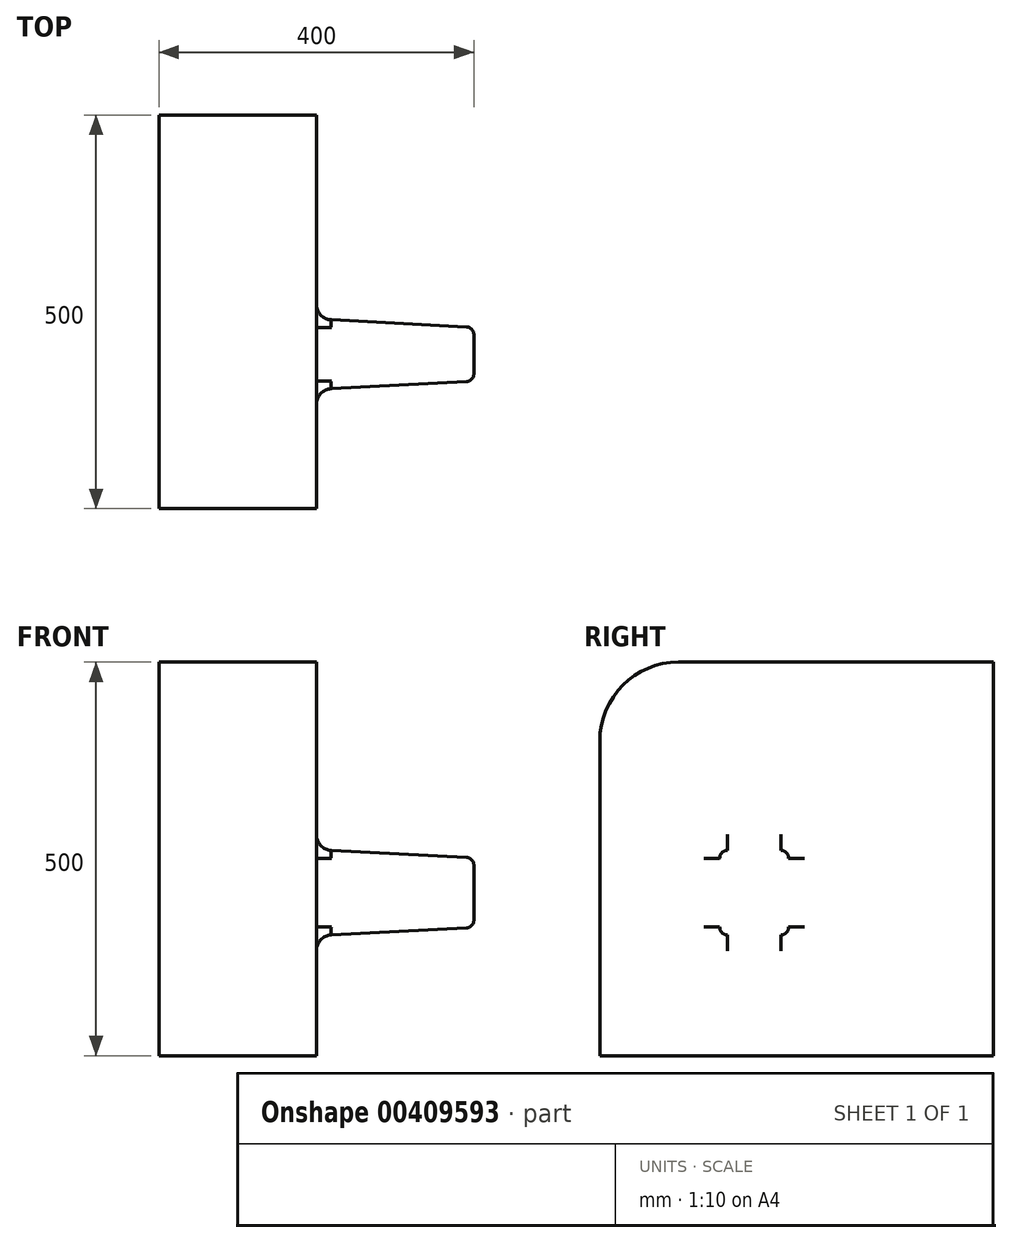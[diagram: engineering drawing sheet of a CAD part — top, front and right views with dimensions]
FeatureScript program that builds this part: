
annotation { "Feature Type Name" : "Feature", "Feature Type Description" : "" }
export const myFeature = defineFeature(function(context is Context, id is Id, definition is map)
    precondition{}
    {
        {
            var Q0;
            Q0=qCreatedBy(makeId("Right.planeOp"),FACE);
            var sketch = newSketch(context, id + "F0", { "sketchPlane" : qUnion([Q0])});
            skLineSegment(sketch, "E0.bottom", {"start": v(-53.94, 67.07) * mm, "end": v(46.06, 67.07) * mm});
            skLineSegment(sketch, "E0.top", {"start": v(-53.94, -52.93) * mm, "end": v(46.06, -52.93) * mm});
            skLineSegment(sketch, "E0.left", {"start": v(-53.94, 67.07) * mm, "end": v(-53.94, -52.93) * mm});
            skLineSegment(sketch, "E0.right", {"start": v(46.06, 67.07) * mm, "end": v(46.06, -52.93) * mm});
            skSolve(sketch);
        }
        {
            var Q0;
            Q0=qCreatedBy(makeId("Right.planeOp"),FACE);
            var sketch = newSketch(context, id + "F1", { "sketchPlane" : qUnion([Q0])});
            skLineSegment(sketch, "E1.bottom", {"start": v(300, 300) * mm, "end": v(-200, 300) * mm});
            skLineSegment(sketch, "E1.top", {"start": v(300, -200) * mm, "end": v(-200, -200) * mm});
            skLineSegment(sketch, "E1.left", {"start": v(300, 300) * mm, "end": v(300, -200) * mm});
            skLineSegment(sketch, "E1.right", {"start": v(-200, 300) * mm, "end": v(-200, -200) * mm});
            skSolve(sketch);
        }
        {
            var Q0;
            Q0=makeQuery(id+"F1.imprint","IMPRINT",FACE,{"disambiguationData":[TD([[makeQuery(id+"F1.imprint","IMPRINT",EDGE,{"derivedFrom":sQuery(id+"F1.wireOp",EDGE,"E1.bottom")}),1.0]])]});
            extrude(context, id + "F2", {"entities" : qUnion([Q0]), "oppositeDirection" : true, "depth" : 100 * mm, "hasSecondDirection" : true, "secondDirectionOppositeDirection" : false, "secondDirectionDepth" : 100 * mm});
        }
        {
            var Q0;
            Q0=makeQuery(id+"F2.opExtrude","SWEPT_EDGE",EDGE,{"disambiguationData":[OSD([sQuery(id+"F1.wireOp",EDGE,"E1.bottom"),sQuery(id+"F1.wireOp",EDGE,"E1.right")])]});
            fillet(context, id + "F3", {"entities" : qUnion([Q0]), "radius" : 100 * mm, "tangentPropagation" : true, "allowEdgeOverflow" : false});
        }
        {
            var Q0;
            Q0 = qSketchRegion(id + "F0", true);
            extrude(context, id + "F4", {"entities" : qUnion([Q0]), "operationType" : NewBodyOperationType.ADD, "depth" : 300 * mm, "offsetDistance" : 25 * mm, "hasDraft" : true, "draftAngle" : 3 * degree, "draftPullDirection" : true});
        }
        {
            var Q0;
            Q0=makeQuery(id+"F4.opExtrude","SWEPT_EDGE",EDGE,{"disambiguationData":[OSD([sQuery(id+"F0.wireOp",EDGE,"E0.top"),sQuery(id+"F0.wireOp",EDGE,"E0.left")])]});
            var Q1;
            Q1=makeQuery(id+"F4.opExtrude","SWEPT_EDGE",EDGE,{"disambiguationData":[OSD([sQuery(id+"F0.wireOp",EDGE,"E0.bottom"),sQuery(id+"F0.wireOp",EDGE,"E0.left")])]});
            var Q2;
            Q2=makeQuery(id+"F4.opExtrude","SWEPT_EDGE",EDGE,{"disambiguationData":[OSD([sQuery(id+"F0.wireOp",EDGE,"E0.top"),sQuery(id+"F0.wireOp",EDGE,"E0.right")])]});
            var Q3;
            Q3=makeQuery(id+"F4.opExtrude","SWEPT_EDGE",EDGE,{"disambiguationData":[OSD([sQuery(id+"F0.wireOp",EDGE,"E0.bottom"),sQuery(id+"F0.wireOp",EDGE,"E0.right")])]});
            fillet(context, id + "F5", {"entities" : qUnion([Q0, Q1, Q2, Q3]), "tangentPropagation" : true, "radius" : 10 * mm, "defaultsChanged" : true, "vertexSettings" : [], "allowEdgeOverflow" : false});
        }
        {
            var Q0;
            Q0=makeQuery(id+"F4.opExtrude","CAP_EDGE",EDGE,{"disambiguationData":[OSD([sQuery(id+"F0.wireOp",EDGE,"E0.right")])],"isStart":false});
            fillet(context, id + "F6", {"entities" : qUnion([Q0]), "tangentPropagation" : true, "radius" : 10 * mm, "defaultsChanged" : true, "vertexSettings" : [], "allowEdgeOverflow" : false});
        }
        {
            var Q0;
            Q0=makeQuery(id+"F4.boolean.opBoolean","INTERSECT",EDGE,{"derivedFrom":[makeQuery(id+"F2.opExtrude","CAP_FACE",FACE,{"disambiguationData":[OSD([sQuery(id+"F1.wireOp",EDGE,"E1.bottom"),sQuery(id+"F1.wireOp",EDGE,"E1.top"),sQuery(id+"F1.wireOp",EDGE,"E1.left"),sQuery(id+"F1.wireOp",EDGE,"E1.right")])],"isStart":true}),makeQuery(id+"F4.opExtrude","SWEPT_FACE",FACE,{"disambiguationData":[OSD([sQuery(id+"F0.wireOp",EDGE,"E0.right")])]})]});
            fillet(context, id + "F7", {"entities" : qUnion([Q0]), "tangentPropagation" : true, "radius" : 20 * mm, "defaultsChanged" : true, "vertexSettings" : [], "allowEdgeOverflow" : false});
        }
    });
